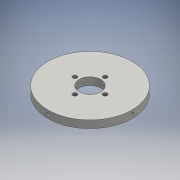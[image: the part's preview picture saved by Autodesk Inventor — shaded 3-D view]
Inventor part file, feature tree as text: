
AUTODESK INVENTOR PART (.ipt)
format: ipt  version: 2016 (Build 200138000, 138)  size: 144,384 bytes
history: native  units: mm
features: extrude x6, sketch x6, other x5, thread x4
ambient origin geometry x8: Origin, YZ Plane, XZ Plane, XY Plane, X Axis, Y Axis, Z Axis, Center Point
bodies: Body1 (feature_tree)
feature tree (21):
  other  "ソリッド1"
  extrude  "押し出し1"  Depth=89.0mm
  extrude  "押し出し2"  Depth=23.0mm
  other  "作業平面1"
  extrude  "押し出し3"  Depth=8.0mm TaperAngle=0.0deg
  other  "作業平面2"
  extrude  "押し出し4"  Depth=16.0mm
  other  "作業平面3"
  extrude  "押し出し5"  Depth=4.5mm
  other  "作業平面4"
  extrude  "押し出し6"  Depth=40.0mm TaperAngle=360.0deg
  thread  "ねじ2"
  thread  "ねじ3"
  thread  "ねじ4"
  thread  "ねじ5"
  sketch  "スケッチ1"
  sketch  "スケッチ2"
  sketch  "スケッチ3"
  sketch  "スケッチ4"
  sketch  "スケッチ5"
  sketch  "スケッチ6"
